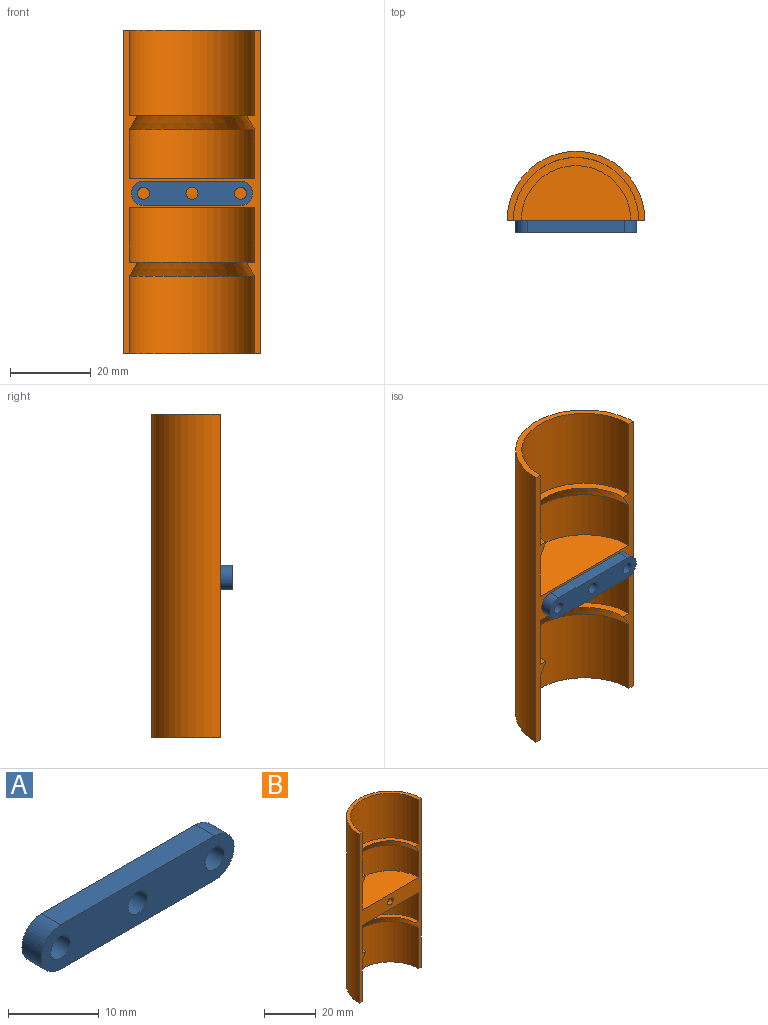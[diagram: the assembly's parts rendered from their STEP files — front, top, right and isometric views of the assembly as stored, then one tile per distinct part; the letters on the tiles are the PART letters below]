
ASSEMBLY  parts=2 mates=1
PART A: 9 faces, bbox 30x3x6 mm
  f0: plane 24x3mm, normal (0,0,1), area 72mm2, adj f1,f5,f7,f8
  f1: cylinder r=3mm len=6mm, axis (0,1,0), area 28.3mm2, adj f0,f2,f7,f8
  f2: plane 24x3mm, normal (0,0,-1), area 72mm2, adj f1,f5,f7,f8
  f3: cylinder r=1.5mm len=3mm, axis (0,1,0), area 28.3mm2, adj f7,f8
  f4: cylinder r=1.5mm len=3mm, axis (0,1,0), area 28.3mm2, adj f7,f8
  f5: cylinder r=3mm len=6mm, axis (0,1,0), area 28.3mm2, adj f0,f2,f7,f8
  f6: cylinder r=1.5mm len=3mm, axis (0,1,0), area 28.3mm2, adj f7,f8
  f7: plane 30x6mm, normal (0,-1,0), area 151.1mm2, adj f0,f1,f2,f3,f4,f5,f6
  f8: plane 30x6mm, normal (0,1,0), area 151.1mm2, adj f0,f1,f2,f3,f4,f5,f6
PART B: 16 faces, bbox 34x17x80 mm
  f0: cylinder r=15.5mm len=31mm, axis (0,0,-1), area 651.8mm2, adj f5,f9,f15
  f1: cylinder r=15.5mm len=31mm, axis (0,0,-1), area 1030.2mm2, adj f5,f6,f12
  f2: cylinder r=15.5mm len=31mm, axis (0,0,-1), area 936mm2, adj f5,f7,f14
  f3: cylinder r=15.5mm len=31mm, axis (0,0,-1), area 589.2mm2, adj f5,f8,f13
  f4: cylinder r=17mm len=80mm, axis (0,0,-1), area 4272.6mm2, adj f5,f6,f7
  f5: plane 80x34mm, normal (0,-1,0), area 470.2mm2, adj f0,f1,f2,f3,f4,f6,f7,f8
  f6: plane 34x17mm, normal (0,0,1), area 76.6mm2, adj f1,f4,f5
  f7: plane 34x17mm, normal (0,0,-1), area 76.6mm2, adj f2,f4,f5
  f8: plane 31x15.5mm, normal (0,0,1), area 377.4mm2, adj f3,f5
  f9: plane 31x15.5mm, normal (0,0,-1), area 377.4mm2, adj f0,f5
  f10: cylinder r=1.5mm len=15.5mm, axis (0,-1,0), area 145.7mm2, adj f5,f11
  f11: cylinder r=15.5mm len=3mm, axis (0,0,-1), area 7.1mm2, adj f10
  f12: plane 31x15.5mm, normal (0,0,1), area 91.1mm2, adj f1,f5,f13
  f13: cone r=13.5mm half-angle=30deg, axis (0,0,-1), area 182.2mm2, adj f3,f5,f12
  f14: cone r=13.5mm half-angle=30deg, axis (0,0,-1), area 182.2mm2, adj f2,f5,f15
  f15: plane 31x15.5mm, normal (0,0,1), area 91.1mm2, adj f0,f5,f14
PLACE A t=(-111.16,4.26,-27.55)mm
PLACE B t=(88.74,-42.94,-1.64)mm
MATE revolute A.f6 <-> B.f10  axis (0,1,0) through (-22.21,4.26,38.04)mm
